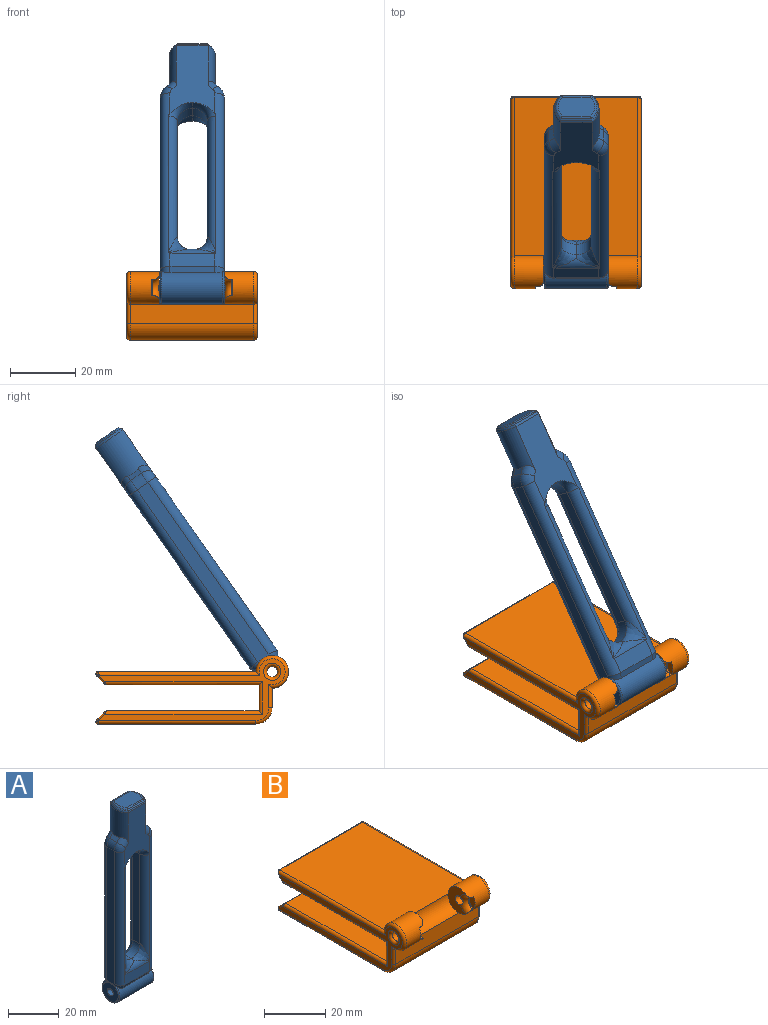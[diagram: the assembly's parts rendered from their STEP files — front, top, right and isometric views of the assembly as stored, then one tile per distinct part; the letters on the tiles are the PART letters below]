
ASSEMBLY  parts=2 mates=1
PART A: 72 faces, bbox 20.4x29.4x94.3 mm
  f0: plane 0.47x0.35mm, normal (0,0,-1), area 0.1mm2, adj f1,f64,f65
  f1: plane 25.35x13.7mm, normal (0,-1,0), area 247.2mm2, adj f0,f15,f16,f26,f36,f37,f38,f40
  f2: plane 25.35x13.7mm, normal (0,1,0), area 247.2mm2, adj f15,f16,f27,f44,f45,f46,f48,f49
  f3: cylinder r=4.9mm len=18.8mm, axis (-1,0,0), area 407.5mm2, adj f4,f5,f12,f13,f35,f39,f43,f47
  f4: torus R=4.4mm, axis (1,0,0), area 20.6mm2, adj f3,f8,f9,f35,f43
  f5: torus R=4.4mm, axis (1,0,0), area 20.6mm2, adj f3,f7,f10,f39,f47
  f6: cylinder r=1.65mm len=19.8mm, axis (-1,0,0), area 106.7mm2, adj f7,f8,f18
  f7: plane 8.8x8.8mm, normal (1,0,0), area 52.3mm2, adj f5,f6
  f8: plane 8.8x8.8mm, normal (-1,0,0), area 52.3mm2, adj f4,f6
  f9: plane 65.01x4mm, normal (-1,0,0), area 259mm2, adj f4,f33,f35,f36,f43,f44
  f10: plane 65.01x4mm, normal (1,0,0), area 259mm2, adj f5,f34,f39,f40,f47,f48
  f11: plane 13.7x4.82mm, normal (0,1,0), area 66mm2, adj f12,f44,f48,f55
  f12: plane 13.7x1.59mm, normal (0,0.87,-0.5), area 25.2mm2, adj f3,f11,f43,f47
  f13: plane 13.7x1.72mm, normal (0,-0.87,-0.5), area 27.2mm2, adj f3,f14,f35,f39
  f14: plane 13.7x4.82mm, normal (0,-1,0), area 66mm2, adj f13,f36,f40,f58
  f15: cylinder r=7mm len=14.88mm, axis (0,0,-1), area 147.2mm2, adj f1,f2,f20,f28,f38,f46
  f16: cylinder r=7mm len=14.88mm, axis (0,0,-1), area 147.2mm2, adj f1,f2,f19,f25,f42,f50
  f17: plane 11.17x7.17mm, normal (0,0,1), area 74.2mm2, adj f29,f30,f31,f32
  f18: cylinder r=1.65mm len=19.7mm, axis (-1,0,0), area 98.5mm2, adj f6
  f19: plane 4.58x2.26mm, normal (0.71,0,0.71), area 8.4mm2, adj f16,f34,f42,f50
  f20: plane 4.58x2.26mm, normal (-0.71,0,0.71), area 8.4mm2, adj f15,f33,f38,f46
  f21: plane 9.56x0.42mm, normal (0,0.71,0.71), area 5.5mm2, adj f22,f23,f27,f31
  f22: cone r=6mm half-angle=45deg, axis (0,0,-1), area 5.8mm2, adj f21,f24,f25,f32
  f23: cone r=6mm half-angle=45deg, axis (0,0,-1), area 5.8mm2, adj f21,f24,f28,f29
  f24: plane 9.56x0.42mm, normal (0,-0.71,0.71), area 5.5mm2, adj f22,f23,f26,f30
  f25: torus R=6mm, axis (0,0,1), area 8.5mm2, adj f16,f22,f26,f27
  f26: cylinder r=1mm len=9.8mm, axis (1,0,0), area 7.6mm2, adj f1,f24,f25,f28
  f27: cylinder r=1mm len=9.8mm, axis (-1,0,0), area 7.6mm2, adj f2,f21,f25,f28
  f28: torus R=6mm, axis (0,0,1), area 8.5mm2, adj f15,f23,f26,f27
  f29: torus R=5.59mm, axis (0,0,1), area 6.8mm2, adj f17,f23,f30,f31
  f30: cylinder r=1mm len=9.2mm, axis (-1,0,0), area 7mm2, adj f17,f24,f29,f32
  f31: cylinder r=1mm len=9.2mm, axis (-1,0,0), area 7mm2, adj f17,f21,f29,f32
  f32: torus R=5.59mm, axis (0,0,1), area 6.8mm2, adj f17,f22,f30,f31
  f33: cylinder r=5mm len=4mm, axis (0,1,0), area 15.7mm2, adj f9,f20,f37,f45
  f34: cylinder r=5mm len=4mm, axis (0,-1,0), area 15.7mm2, adj f10,f19,f41,f49
  f35: cylinder r=3mm len=3.59mm, axis (0,0.5,-0.87), area 6.2mm2, adj f3,f4,f9,f13,f36
  f36: cylinder r=3mm len=64.93mm, axis (0,0,-1), area 285.4mm2, adj f1,f9,f14,f35,f37,f58,f59,f64
  f37: torus R=2mm, axis (0,-1,0), area 14.5mm2, adj f1,f33,f36,f38
  f38: cylinder r=3mm len=3.8mm, axis (0.71,0,0.71), area 10.1mm2, adj f1,f15,f20,f37
  f39: cylinder r=3mm len=3.59mm, axis (0,-0.5,0.87), area 6.2mm2, adj f3,f5,f10,f13,f40
  f40: cylinder r=3mm len=64.93mm, axis (0,0,1), area 285.4mm2, adj f1,f10,f14,f39,f41,f57,f58,f65
  f41: torus R=2mm, axis (0,-1,0), area 14.5mm2, adj f1,f34,f40,f42
  f42: cylinder r=3mm len=3.8mm, axis (-0.71,0,0.71), area 10.1mm2, adj f1,f16,f19,f41
  f43: cylinder r=3mm len=3.52mm, axis (0,0.5,0.87), area 5.7mm2, adj f3,f4,f9,f12,f44
  f44: cylinder r=3mm len=64.93mm, axis (0,0,1), area 285.4mm2, adj f2,f9,f11,f43,f45,f54,f55,f60
  f45: torus R=2mm, axis (0,-1,0), area 14.5mm2, adj f2,f33,f44,f46
  f46: cylinder r=3mm len=3.8mm, axis (0.71,0,0.71), area 10.1mm2, adj f2,f15,f20,f45
  f47: cylinder r=3mm len=3.52mm, axis (0,-0.5,-0.87), area 5.7mm2, adj f3,f5,f10,f12,f48
  f48: cylinder r=3mm len=64.93mm, axis (0,0,-1), area 285.4mm2, adj f2,f10,f11,f47,f49,f55,f56,f61
  f49: torus R=2mm, axis (0,-1,0), area 14.5mm2, adj f2,f34,f48,f50
  f50: cylinder r=3mm len=3.8mm, axis (-0.71,0,0.71), area 10.1mm2, adj f2,f16,f19,f49
  f51: plane 43.48x4mm, normal (-1,0,0), area 173.9mm2, adj f56,f57,f63,f69
  f52: plane 0.47x0.35mm, normal (0,0,-1), area 0.1mm2, adj f2,f60,f61
  f53: plane 43.48x4mm, normal (1,0,0), area 173.9mm2, adj f54,f59,f62,f71
  f54: cylinder r=3mm len=50.49mm, axis (0,0,-1), area 204mm2, adj f44,f53,f60,f68
  f55: cylinder r=3mm len=14.1mm, axis (1,0,0), area 23.9mm2, adj f11,f44,f48,f66,f68
  f56: cylinder r=3mm len=50.49mm, axis (0,0,1), area 204mm2, adj f48,f51,f61,f66
  f57: cylinder r=3mm len=50.49mm, axis (0,0,-1), area 204mm2, adj f40,f51,f65,f67
  f58: cylinder r=3mm len=14.1mm, axis (-1,0,0), area 23.9mm2, adj f14,f36,f40,f67,f70
  f59: cylinder r=3mm len=50.49mm, axis (0,0,1), area 204mm2, adj f36,f53,f64,f70
  f60: torus R=8mm, axis (0,0,1), area 26.6mm2, adj f2,f44,f52,f54,f61,f62
  f61: torus R=8mm, axis (0,0,1), area 26.6mm2, adj f2,f48,f52,f56,f60,f63
  f62: cylinder r=5mm len=4.98mm, axis (0,-1,0), area 29.8mm2, adj f53,f60,f63,f64
  f63: cylinder r=5mm len=4.98mm, axis (0,1,0), area 29.8mm2, adj f51,f61,f62,f65
  f64: torus R=8mm, axis (0,0,1), area 26.6mm2, adj f0,f1,f36,f59,f62,f65
  f65: torus R=8mm, axis (0,0,1), area 26.6mm2, adj f0,f1,f40,f57,f63,f64
  f66: bspline ~8x8mm, area 29.5mm2, adj f48,f55,f56,f68,f69
  f67: bspline ~7.8x7.8mm, area 29.5mm2, adj f40,f57,f58,f69,f70
  f68: bspline ~7.8x7.8mm, area 29.5mm2, adj f44,f54,f55,f66,f71
  f69: cylinder r=5mm len=4.98mm, axis (0,-1,0), area 29.8mm2, adj f51,f66,f67,f71
  f70: bspline ~8x8mm, area 29.5mm2, adj f36,f58,f59,f67,f71
  f71: cylinder r=5mm len=4.98mm, axis (0,1,0), area 29.8mm2, adj f53,f68,f69,f70
PART B: 70 faces, bbox 40x59.4x22.6 mm
  f0: cylinder r=5mm len=10mm, axis (-1,0,0), area 197.7mm2, adj f6,f7,f15,f22,f66,f67,f68
  f1: cylinder r=5mm len=10mm, axis (-1,0,0), area 197.7mm2, adj f6,f7,f16,f31,f64,f65,f69
  f2: plane 57x19mm, normal (1,0,0), area 244.2mm2, adj f19,f30,f31,f32,f33,f34,f35,f36
  f3: plane 57x19mm, normal (-1,0,0), area 244.2mm2, adj f20,f21,f22,f23,f24,f25,f26,f27
  f4: plane 39x2.71mm, normal (0,0.71,-0.71), area 149mm2, adj f39,f40,f41,f42,f43,f44,f45,f46
  f5: plane 39x2.71mm, normal (0,0.71,0.71), area 149mm2, adj f47,f48,f49,f50,f51,f52,f53,f54
  f6: plane 48.5x38mm, normal (0,0,1), area 1841.9mm2, adj f0,f1,f14,f15,f16,f21,f30,f56
  f7: plane 38x6mm, normal (0,-1,0), area 227.4mm2, adj f0,f1,f14,f15,f16,f24,f33,f62
  f8: plane 38x8mm, normal (0,1,0), area 304mm2, adj f9,f13,f27,f36
  f9: plane 46.79x38mm, normal (0,0,-1), area 1778.1mm2, adj f8,f25,f34,f43
  f10: plane 38x0.29mm, normal (0,1,0), area 11.1mm2, adj f23,f32,f42,f56
  f11: plane 48.5x38mm, normal (0,0,-1), area 1843mm2, adj f26,f35,f59,f62
  f12: plane 38x0.29mm, normal (0,1,0), area 11.1mm2, adj f28,f37,f51,f59
  f13: plane 46.79x38mm, normal (0,0,1), area 1778.1mm2, adj f8,f29,f38,f50
  f14: cylinder r=5.05mm len=20mm, axis (1,0,0), area 158.4mm2, adj f6,f7,f15,f16
  f15: plane 10.03x8.09mm, normal (1,0,0), area 47.3mm2, adj f0,f6,f7,f14,f18,f68
  f16: plane 10.03x8.09mm, normal (-1,0,0), area 47.3mm2, adj f1,f6,f7,f14,f17,f69
  f17: cylinder r=1.65mm len=9mm, axis (1,0,0), area 92.7mm2, adj f16,f19,f69
  f18: cylinder r=1.65mm len=9mm, axis (1,0,0), area 92.7mm2, adj f15,f20,f68
  f19: torus R=2.65mm, axis (1,0,0), area 19.9mm2, adj f2,f17
  f20: torus R=2.65mm, axis (1,0,0), area 19.9mm2, adj f3,f18
  f21: cylinder r=1mm len=49.63mm, axis (0,-1,0), area 76.5mm2, adj f3,f6,f22,f55
  f22: torus R=4mm, axis (1,0,0), area 35.5mm2, adj f0,f3,f21,f24
  f23: cylinder r=1mm len=1mm, axis (0,0,1), area 0.5mm2, adj f3,f10,f40,f55
  f24: cylinder r=1mm len=7.13mm, axis (0,0,-1), area 10mm2, adj f3,f7,f22,f63
  f25: cylinder r=1mm len=48.29mm, axis (0,1,0), area 74.4mm2, adj f3,f9,f27,f41
  f26: cylinder r=1mm len=48.5mm, axis (0,1,0), area 75.9mm2, adj f3,f11,f58,f63
  f27: cylinder r=1mm len=10mm, axis (0,0,1), area 13.7mm2, adj f3,f8,f25,f29
  f28: cylinder r=1mm len=1mm, axis (0,0,1), area 0.5mm2, adj f3,f12,f49,f58
  f29: cylinder r=1mm len=48.29mm, axis (0,-1,0), area 74.4mm2, adj f3,f13,f27,f48
  f30: cylinder r=1mm len=49.63mm, axis (0,1,0), area 76.5mm2, adj f2,f6,f31,f57
  f31: torus R=4mm, axis (1,0,0), area 35.5mm2, adj f1,f2,f30,f33
  f32: cylinder r=1mm len=1mm, axis (0,0,-1), area 0.5mm2, adj f2,f10,f44,f57
  f33: cylinder r=1mm len=7.13mm, axis (0,0,1), area 10mm2, adj f2,f7,f31,f61
  f34: cylinder r=1mm len=48.29mm, axis (0,-1,0), area 74.4mm2, adj f2,f9,f36,f45
  f35: cylinder r=1mm len=48.5mm, axis (0,-1,0), area 75.9mm2, adj f2,f11,f60,f61
  f36: cylinder r=1mm len=10mm, axis (0,0,-1), area 13.7mm2, adj f2,f8,f34,f38
  f37: cylinder r=1mm len=1mm, axis (0,0,-1), area 0.5mm2, adj f2,f12,f53,f60
  f38: cylinder r=1mm len=48.29mm, axis (0,1,0), area 74.4mm2, adj f2,f13,f36,f52
  f39: cylinder r=0.5mm len=2.06mm, axis (0,0.71,0.71), area 1.9mm2, adj f3,f4,f40,f41
  f40: bspline ~1x1mm, area 0.7mm2, adj f4,f23,f39,f42
  f41: bspline ~1x1mm, area 0.7mm2, adj f4,f25,f39,f43
  f42: cylinder r=0.5mm len=38mm, axis (-1,0,0), area 14.9mm2, adj f4,f10,f40,f44
  f43: cylinder r=0.5mm len=38mm, axis (1,0,0), area 14.9mm2, adj f4,f9,f41,f45
  f44: bspline ~1x1mm, area 0.7mm2, adj f4,f32,f42,f46
  f45: bspline ~1x1mm, area 0.7mm2, adj f4,f34,f43,f46
  f46: cylinder r=0.5mm len=2.06mm, axis (0,0.71,0.71), area 1.9mm2, adj f2,f4,f44,f45
  f47: cylinder r=0.5mm len=2.06mm, axis (0,0.71,-0.71), area 1.9mm2, adj f3,f5,f48,f49
  f48: bspline ~1x1mm, area 0.7mm2, adj f5,f29,f47,f50
  f49: bspline ~1x1mm, area 0.7mm2, adj f5,f28,f47,f51
  f50: cylinder r=0.5mm len=38mm, axis (1,0,0), area 14.9mm2, adj f5,f13,f48,f52
  f51: cylinder r=0.5mm len=38mm, axis (-1,0,0), area 14.9mm2, adj f5,f12,f49,f53
  f52: bspline ~1x1mm, area 0.7mm2, adj f5,f38,f50,f54
  f53: bspline ~1x1mm, area 0.7mm2, adj f5,f37,f51,f54
  f54: cylinder r=0.5mm len=2.06mm, axis (0,-0.71,0.71), area 1.9mm2, adj f2,f5,f52,f53
  f55: bspline ~1.19x1mm, area 0.8mm2, adj f21,f23,f56
  f56: cylinder r=0.5mm len=38mm, axis (1,0,0), area 29.8mm2, adj f6,f10,f55,f57
  f57: bspline ~1.19x1mm, area 0.8mm2, adj f30,f32,f56
  f58: bspline ~1.19x1mm, area 0.8mm2, adj f26,f28,f59
  f59: cylinder r=0.5mm len=38mm, axis (1,0,0), area 29.8mm2, adj f11,f12,f58,f60
  f60: bspline ~1.19x1mm, area 0.8mm2, adj f35,f37,f59
  f61: torus R=4mm, axis (1,0,0), area 11.4mm2, adj f2,f33,f35,f62
  f62: cylinder r=5mm len=38mm, axis (1,0,0), area 298.5mm2, adj f7,f11,f61,f63
  f63: torus R=4mm, axis (1,0,0), area 11.4mm2, adj f3,f24,f26,f62
  f64: cylinder r=2.5mm len=4.83mm, axis (-1,0,0), area 3.3mm2, adj f1,f65,f69
  f65: plane 4.83x2.47mm, normal (-1,0,0), area 8.6mm2, adj f1,f64
  f66: plane 4.83x2.47mm, normal (1,0,0), area 8.6mm2, adj f0,f67
  f67: cylinder r=2.5mm len=4.83mm, axis (-1,0,0), area 3.3mm2, adj f0,f66,f68
  f68: torus R=4.5mm, axis (1,0,0), area 22.3mm2, adj f0,f15,f18,f67
  f69: torus R=4.5mm, axis (1,0,0), area 22.3mm2, adj f1,f16,f17,f64
PLACE A rot(axis=(-1,0,0),35deg) t=(-2.09,-36.06,-0.19)mm
PLACE B rot(axis=(0.14,0.13,-0.98),0deg) t=(-2.19,-30.74,0.65)mm fixed
MATE revolute A.f3 <-> B.f17  axis (1,0,0) through (7.81,-34.75,8.67)mm
